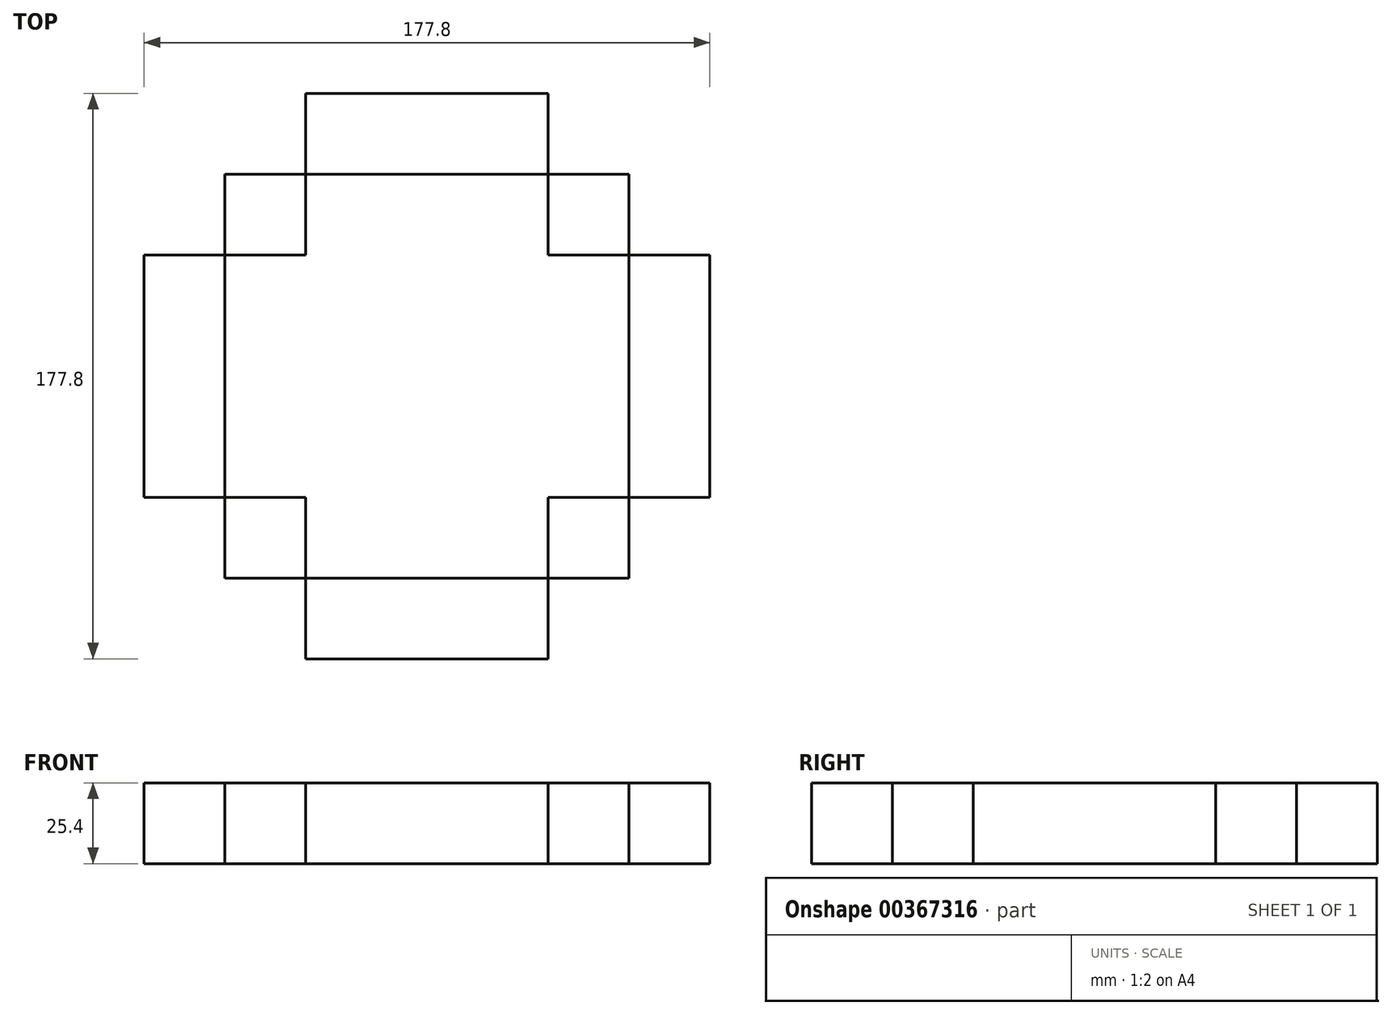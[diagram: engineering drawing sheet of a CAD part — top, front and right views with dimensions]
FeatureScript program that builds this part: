
annotation { "Feature Type Name" : "Feature", "Feature Type Description" : "" }
export const myFeature = defineFeature(function(context is Context, id is Id, definition is map)
    precondition{}
    {
        {
            var Q0;
            Q0=qCreatedBy(makeId("Top.planeOp"),FACE);
            var sketch = newSketch(context, id + "F0", { "sketchPlane" : qUnion([Q0])});
            skLineSegment(sketch, "E0.bottom", {"start": v(-88.9, 88.9) * mm, "end": v(88.9, 88.9) * mm});
            skLineSegment(sketch, "E0.top", {"start": v(-88.9, -88.9) * mm, "end": v(88.9, -88.9) * mm});
            skLineSegment(sketch, "E0.left", {"start": v(-88.9, 88.9) * mm, "end": v(-88.9, -88.9) * mm});
            skLineSegment(sketch, "E0.right", {"start": v(88.9, 88.9) * mm, "end": v(88.9, -88.9) * mm});
            skSolve(sketch);
        }
        {
            var Q0;
            Q0=makeQuery(id+"F0.imprint","IMPRINT",FACE,{"disambiguationData":[TD([[makeQuery(id+"F0.imprint","IMPRINT",EDGE,{"derivedFrom":sQuery(id+"F0.wireOp",EDGE,"E0.bottom")}),-1.0]])]});
            var sketch = newSketch(context, id + "F1", { "sketchPlane" : qUnion([Q0])});
            skLineSegment(sketch, "E1.bottom", {"start": v(-88.9, 38.1) * mm, "end": v(-63.5, 38.1) * mm});
            skLineSegment(sketch, "E1.top", {"start": v(-88.9, -38.1) * mm, "end": v(-63.5, -38.1) * mm});
            skLineSegment(sketch, "E1.left", {"start": v(-88.9, 38.1) * mm, "end": v(-88.9, -38.1) * mm});
            skLineSegment(sketch, "E1.right", {"start": v(-63.5, 38.1) * mm, "end": v(-63.5, -38.1) * mm});
            skLineSegment(sketch, "E2.bottom", {"start": v(-38.1, 88.9) * mm, "end": v(38.1, 88.9) * mm});
            skLineSegment(sketch, "E2.top", {"start": v(-38.1, 63.5) * mm, "end": v(38.1, 63.5) * mm});
            skLineSegment(sketch, "E2.left", {"start": v(-38.1, 88.9) * mm, "end": v(-38.1, 63.5) * mm});
            skLineSegment(sketch, "E2.right", {"start": v(38.1, 88.9) * mm, "end": v(38.1, 63.5) * mm});
            skLineSegment(sketch, "E3.bottom", {"start": v(63.5, 38.1) * mm, "end": v(88.9, 38.1) * mm});
            skLineSegment(sketch, "E3.top", {"start": v(63.5, -38.1) * mm, "end": v(88.9, -38.1) * mm});
            skLineSegment(sketch, "E3.left", {"start": v(63.5, 38.1) * mm, "end": v(63.5, -38.1) * mm});
            skLineSegment(sketch, "E3.right", {"start": v(88.9, 38.1) * mm, "end": v(88.9, -38.1) * mm});
            skLineSegment(sketch, "E4.bottom", {"start": v(-38.1, -63.5) * mm, "end": v(38.1, -63.5) * mm});
            skLineSegment(sketch, "E4.top", {"start": v(-38.1, -88.9) * mm, "end": v(38.1, -88.9) * mm});
            skLineSegment(sketch, "E4.left", {"start": v(-38.1, -63.5) * mm, "end": v(-38.1, -88.9) * mm});
            skLineSegment(sketch, "E4.right", {"start": v(38.1, -63.5) * mm, "end": v(38.1, -88.9) * mm});
            skLineSegment(sketch, "E5.bottom", {"start": v(38.1, -38.1) * mm, "end": v(63.5, -38.1) * mm});
            skLineSegment(sketch, "E5.top", {"start": v(38.1, -63.5) * mm, "end": v(63.5, -63.5) * mm});
            skLineSegment(sketch, "E5.left", {"start": v(38.1, -38.1) * mm, "end": v(38.1, -63.5) * mm});
            skLineSegment(sketch, "E5.right", {"start": v(63.5, -38.1) * mm, "end": v(63.5, -63.5) * mm});
            skLineSegment(sketch, "E6.bottom", {"start": v(-63.5, -38.1) * mm, "end": v(-38.1, -38.1) * mm});
            skLineSegment(sketch, "E6.top", {"start": v(-63.5, -63.5) * mm, "end": v(-38.1, -63.5) * mm});
            skLineSegment(sketch, "E6.left", {"start": v(-63.5, -38.1) * mm, "end": v(-63.5, -63.5) * mm});
            skLineSegment(sketch, "E6.right", {"start": v(-38.1, -38.1) * mm, "end": v(-38.1, -63.5) * mm});
            skLineSegment(sketch, "E7.bottom", {"start": v(-63.5, 63.5) * mm, "end": v(-38.1, 63.5) * mm});
            skLineSegment(sketch, "E7.top", {"start": v(-63.5, 38.1) * mm, "end": v(-38.1, 38.1) * mm});
            skLineSegment(sketch, "E7.left", {"start": v(-63.5, 63.5) * mm, "end": v(-63.5, 38.1) * mm});
            skLineSegment(sketch, "E7.right", {"start": v(-38.1, 63.5) * mm, "end": v(-38.1, 38.1) * mm});
            skLineSegment(sketch, "E8.bottom", {"start": v(38.1, 63.5) * mm, "end": v(63.5, 63.5) * mm});
            skLineSegment(sketch, "E8.top", {"start": v(38.1, 38.1) * mm, "end": v(63.5, 38.1) * mm});
            skLineSegment(sketch, "E8.left", {"start": v(38.1, 63.5) * mm, "end": v(38.1, 38.1) * mm});
            skLineSegment(sketch, "E8.right", {"start": v(63.5, 63.5) * mm, "end": v(63.5, 38.1) * mm});
            skSolve(sketch);
        }
        {
            var Q0;
            Q0=makeQuery(id+"F1.imprint","IMPRINT",FACE,{"disambiguationData":[TD([[makeQuery(id+"F1.imprint","IMPRINT",EDGE,{"derivedFrom":sQuery(id+"F1.wireOp",EDGE,"E6.bottom")}),-1.0]])]});
            var Q1;
            Q1=makeQuery(id+"F1.imprint","IMPRINT",FACE,{"disambiguationData":[TD([[makeQuery(id+"F1.imprint","IMPRINT",EDGE,{"derivedFrom":sQuery(id+"F1.wireOp",EDGE,"E1.bottom")}),-1.0]])]});
            var Q2;
            Q2=makeQuery(id+"F1.imprint","IMPRINT",FACE,{"disambiguationData":[TD([[makeQuery(id+"F1.imprint","IMPRINT",EDGE,{"derivedFrom":sQuery(id+"F1.wireOp",EDGE,"E7.bottom")}),-1.0]])]});
            var Q3;
            Q3=makeQuery(id+"F1.imprint","IMPRINT",FACE,{"disambiguationData":[TD([[makeQuery(id+"F1.imprint","IMPRINT",EDGE,{"derivedFrom":sQuery(id+"F1.wireOp",EDGE,"E5.bottom")}),-1.0]])]});
            var Q4;
            Q4=makeQuery(id+"F1.imprint","IMPRINT",FACE,{"disambiguationData":[TD([[makeQuery(id+"F1.imprint","IMPRINT",EDGE,{"derivedFrom":sQuery(id+"F1.wireOp",EDGE,"E4.bottom")}),-1.0]])]});
            var Q5;
            Q5=makeQuery(id+"F1.imprint","IMPRINT",FACE,{"disambiguationData":[TD([[makeQuery(id+"F1.imprint","IMPRINT",EDGE,{"derivedFrom":sQuery(id+"F1.wireOp",EDGE,"E3.bottom")}),-1.0]])]});
            var Q6;
            Q6=makeQuery(id+"F1.imprint","IMPRINT",FACE,{"disambiguationData":[TD([[makeQuery(id+"F1.imprint","IMPRINT",EDGE,{"derivedFrom":sQuery(id+"F1.wireOp",EDGE,"E2.bottom")}),-1.0]])]});
            var Q7;
            Q7=makeQuery(id+"F1.imprint","IMPRINT",FACE,{"disambiguationData":[TD([[makeQuery(id+"F1.imprint","IMPRINT",EDGE,{"derivedFrom":sQuery(id+"F1.wireOp",EDGE,"E8.bottom")}),-1.0]])]});
            extrude(context, id + "F2", {"entities" : qUnion([Q0, Q1, Q2, Q3, Q4, Q5, Q6, Q7]), "depth" : 25.4 * mm});
        }
    });
